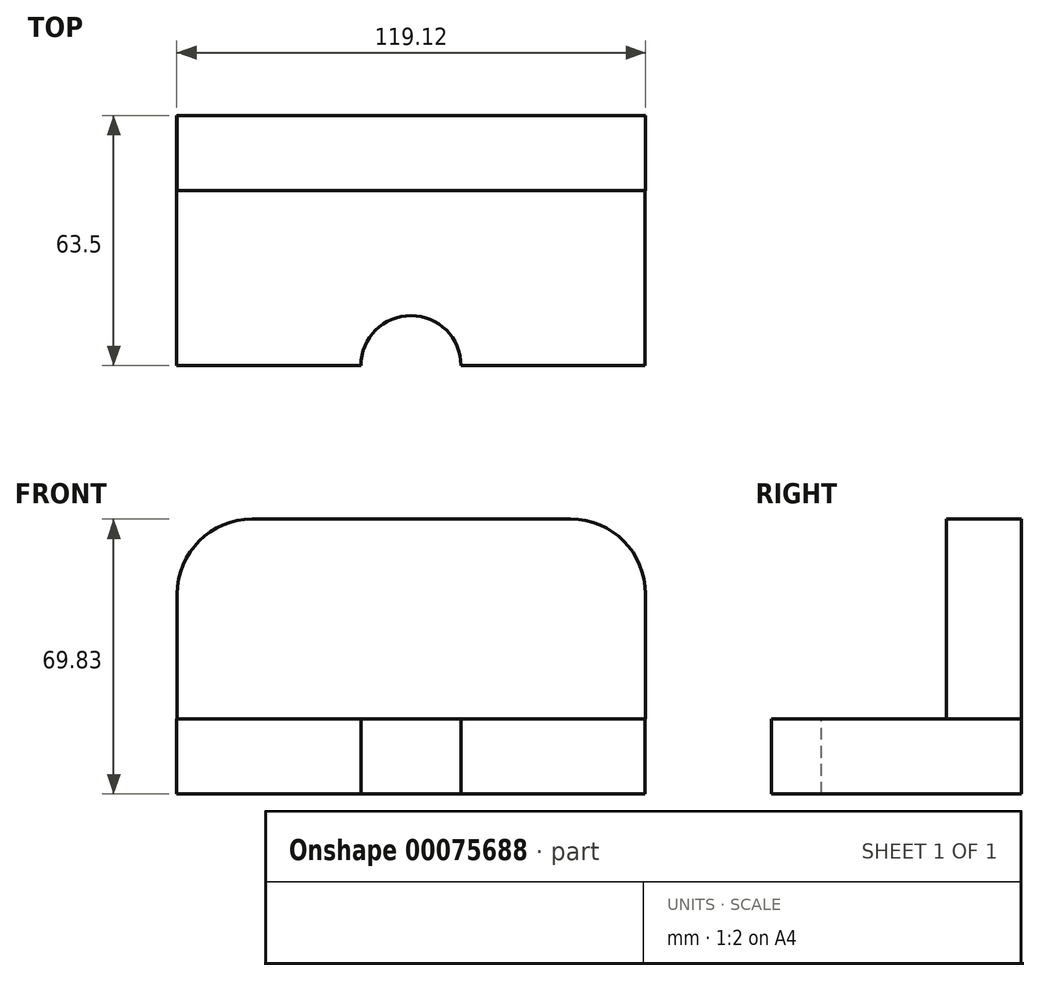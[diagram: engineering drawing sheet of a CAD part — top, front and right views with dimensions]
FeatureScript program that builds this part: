
annotation { "Feature Type Name" : "Feature", "Feature Type Description" : "" }
export const myFeature = defineFeature(function(context is Context, id is Id, definition is map)
    precondition{}
    {
        {
            var Q0;
            Q0=qCreatedBy(makeId("Front.planeOp"),FACE);
            var sketch = newSketch(context, id + "F0", { "sketchPlane" : qUnion([Q0])});
            skLineSegment(sketch, "E0.bottom", {"start": v(-59.57, 0) * mm, "end": v(59.45, 0) * mm});
            skLineSegment(sketch, "E0.top", {"start": v(-59.57, 19.05) * mm, "end": v(59.45, 19.05) * mm});
            skLineSegment(sketch, "E0.left", {"start": v(-59.57, 0) * mm, "end": v(-59.57, 19.05) * mm});
            skLineSegment(sketch, "E0.right", {"start": v(59.45, 0) * mm, "end": v(59.45, 19.05) * mm});
            skSolve(sketch);
        }
        {
            var Q0;
            Q0=makeQuery(id+"F0.imprint","IMPRINT",FACE,{"disambiguationData":[TD([[makeQuery(id+"F0.imprint","IMPRINT",EDGE,{"derivedFrom":sQuery(id+"F0.wireOp",EDGE,"E0.bottom")}),1.0]])]});
            extrude(context, id + "F1", {"entities" : qUnion([Q0]), "depth" : 63.5 * mm});
        }
        {
            var Q0;
            Q0=qCreatedBy(makeId("Front.planeOp"),FACE);
            var sketch = newSketch(context, id + "F2", { "sketchPlane" : qUnion([Q0])});
            skLineSegment(sketch, "E1.bottom", {"start": v(59.55, 19.03) * mm, "end": v(-59.43, 19.03) * mm});
            skLineSegment(sketch, "E1.top", {"start": v(59.55, 69.83) * mm, "end": v(-59.43, 69.83) * mm});
            skLineSegment(sketch, "E1.left", {"start": v(59.55, 19.03) * mm, "end": v(59.55, 69.83) * mm});
            skLineSegment(sketch, "E1.right", {"start": v(-59.43, 19.03) * mm, "end": v(-59.43, 69.83) * mm});
            skSolve(sketch);
        }
        {
            var Q0;
            Q0=makeQuery(id+"F2.imprint","IMPRINT",FACE,{"disambiguationData":[TD([[makeQuery(id+"F2.imprint","IMPRINT",EDGE,{"derivedFrom":sQuery(id+"F2.wireOp",EDGE,"E1.bottom")}),-1.0]])]});
            extrude(context, id + "F3", {"entities" : qUnion([Q0]), "operationType" : NewBodyOperationType.ADD, "depth" : 19.05 * mm});
        }
        {
            var Q0;
            Q0=makeQuery(id+"F1.opExtrude","SWEPT_FACE",FACE,{"disambiguationData":[OSD([sQuery(id+"F0.wireOp",EDGE,"E0.top")])]});
            var sketch = newSketch(context, id + "F4", { "sketchPlane" : qUnion([Q0])});
            skCircle(sketch, "E2", {"center": v(-0.06, -63.5) * mm, "radius": 12.7 * mm});
            skSolve(sketch);
        }
        {
            var Q0;
            {var subQ0=sQuery(id+"F4.wireOp",EDGE,"E2");var subQ1=makeQuery(id+"F1.opExtrude","CAP_EDGE",EDGE,{"disambiguationData":[OSD([sQuery(id+"F0.wireOp",EDGE,"E0.top")])],"isStart":false});var subQ2=makeQuery(id+"F4.imprint","INTERSECT",VERTEX,{"disambiguationData":[OD(0.0)],"derivedFrom":[subQ1,subQ0]});Q0=makeQuery(id+"F4.imprint","IMPRINT",FACE,{"disambiguationData":[TD([[makeQuery(id+"F4.imprint","IMPRINT",EDGE,{"disambiguationData":[TD([[subQ2,1.0]])],"derivedFrom":subQ0}),1.0]])]});}
            extrude(context, id + "F5", {"entities" : qUnion([Q0]), "operationType" : NewBodyOperationType.REMOVE, "oppositeDirection" : true, "depth" : 25.4 * mm});
        }
        {
            var Q0;
            Q0=makeQuery(id+"F3.opExtrude","SWEPT_EDGE",EDGE,{"disambiguationData":[OSD([sQuery(id+"F2.wireOp",EDGE,"E1.top"),sQuery(id+"F2.wireOp",EDGE,"E1.right")])]});
            fillet(context, id + "F6", {"entities" : qUnion([Q0]), "radius" : 19.05 * mm, "tangentPropagation" : true, "allowEdgeOverflow" : false});
        }
        {
            var Q0;
            Q0=makeQuery(id+"F3.opExtrude","SWEPT_EDGE",EDGE,{"disambiguationData":[OSD([sQuery(id+"F2.wireOp",EDGE,"E1.top"),sQuery(id+"F2.wireOp",EDGE,"E1.left")])]});
            fillet(context, id + "F7", {"entities" : qUnion([Q0]), "radius" : 19.05 * mm, "tangentPropagation" : true, "allowEdgeOverflow" : false});
        }
    });
